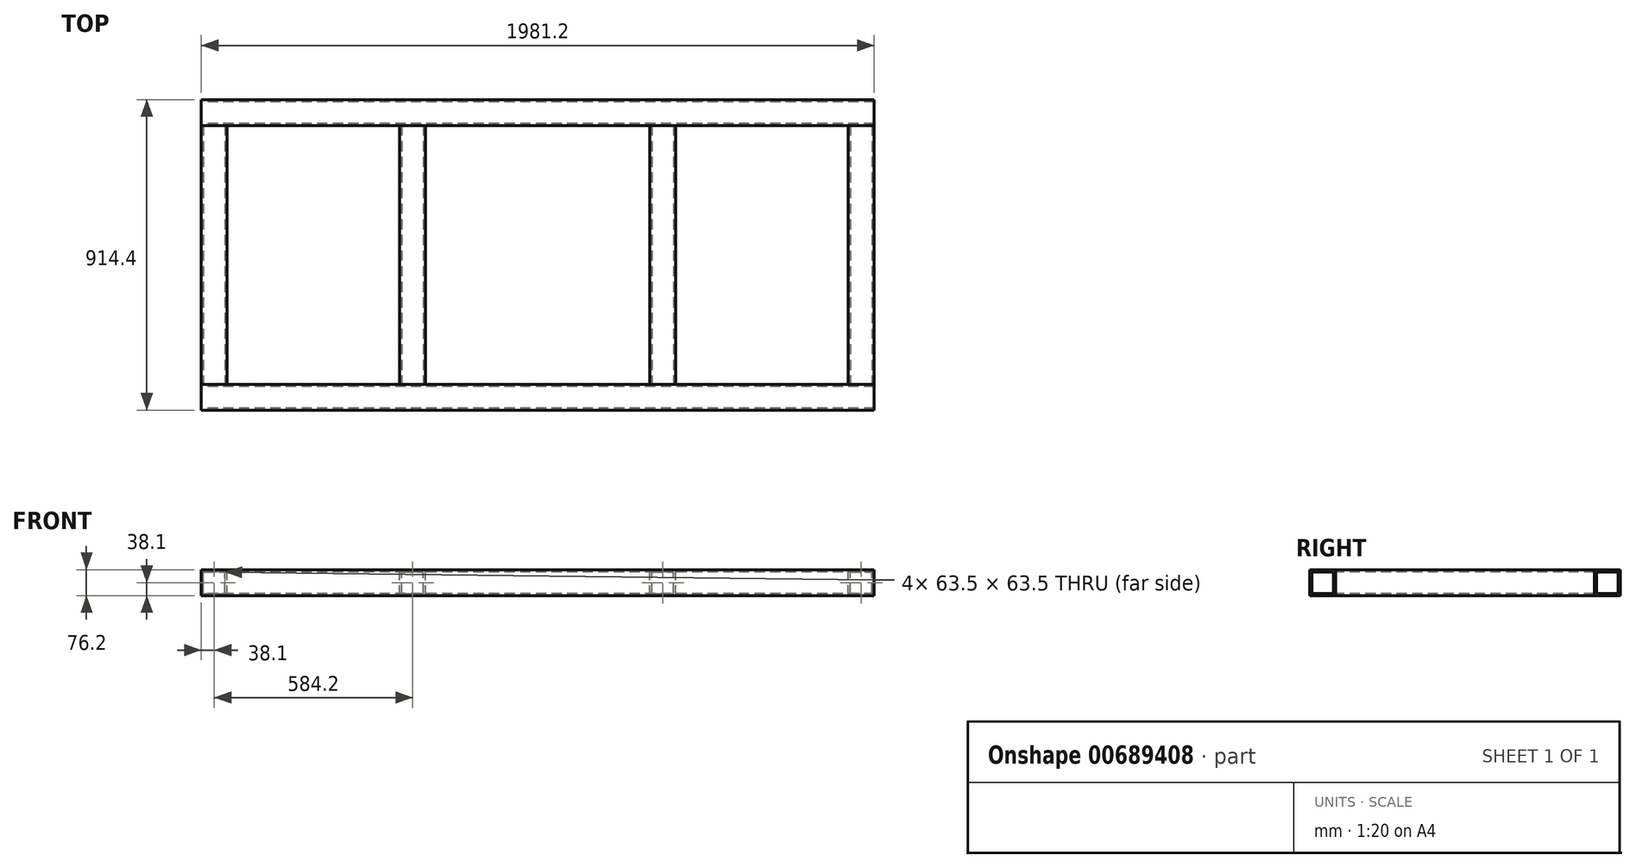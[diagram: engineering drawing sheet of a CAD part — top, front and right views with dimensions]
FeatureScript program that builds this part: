
annotation { "Feature Type Name" : "Feature", "Feature Type Description" : "" }
export const myFeature = defineFeature(function(context is Context, id is Id, definition is map)
    precondition{}
    {
        {
            var Q0;
            Q0=qCreatedBy(makeId("Right.planeOp"),FACE);
            var sketch = newSketch(context, id + "F0", { "sketchPlane" : qUnion([Q0])});
            skLineSegment(sketch, "E0.bottom", {"start": v(0, 0) * mm, "end": v(76.2, 0) * mm});
            skLineSegment(sketch, "E0.top", {"start": v(0, 76.2) * mm, "end": v(76.2, 76.2) * mm});
            skLineSegment(sketch, "E0.left", {"start": v(0, 0) * mm, "end": v(0, 76.2) * mm});
            skLineSegment(sketch, "E0.right", {"start": v(76.2, 0) * mm, "end": v(76.2, 76.2) * mm});
            skLineSegment(sketch, "E1.bottom", {"start": v(6.35, 6.35) * mm, "end": v(69.85, 6.35) * mm});
            skLineSegment(sketch, "E1.top", {"start": v(6.35, 69.85) * mm, "end": v(69.85, 69.85) * mm});
            skLineSegment(sketch, "E1.left", {"start": v(6.35, 6.35) * mm, "end": v(6.35, 69.85) * mm});
            skLineSegment(sketch, "E1.right", {"start": v(69.85, 6.35) * mm, "end": v(69.85, 69.85) * mm});
            skSolve(sketch);
        }
        {
            var Q0;
            Q0=makeQuery(id+"F0.imprint","IMPRINT",FACE,{"disambiguationData":[TD([[makeQuery(id+"F0.imprint","IMPRINT",EDGE,{"derivedFrom":sQuery(id+"F0.wireOp",EDGE,"E0.bottom")}),1.0]])]});
            extrude(context, id + "F1", {"entities" : qUnion([Q0]), "depth" : 1981.2 * mm, "offsetDistance" : 25.4 * mm});
        }
        {
            var Q0;
            Q0=makeQuery(id+"F1.opExtrude","SWEPT_BODY",BODY,{"disambiguationData":[OSD([sQuery(id+"F0.wireOp",EDGE,"E0.bottom"),sQuery(id+"F0.wireOp",EDGE,"E0.top"),sQuery(id+"F0.wireOp",EDGE,"E0.left"),sQuery(id+"F0.wireOp",EDGE,"E0.right"),sQuery(id+"F0.wireOp",EDGE,"E1.bottom"),sQuery(id+"F0.wireOp",EDGE,"E1.top"),sQuery(id+"F0.wireOp",EDGE,"E1.left"),sQuery(id+"F0.wireOp",EDGE,"E1.right")])]});
            var Q1;
            Q1=qCreatedBy(makeId("Front.planeOp"),FACE);
            transform(context, id + "F2", {"entities" : qUnion([Q0]), "transformType" : TransformType.TRANSLATION_DISTANCE, "transformDirection" : qUnion([Q1]), "distance" : 838.2 * mm, "oppositeDirection" : true, "makeCopy" : true});
        }
        {
            var Q0;
            Q0=qCreatedBy(makeId("Front.planeOp"),FACE);
            var sketch = newSketch(context, id + "F3", { "sketchPlane" : qUnion([Q0])});
            skLineSegment(sketch, "E2.bottom", {"start": v(0, 0) * mm, "end": v(76.2, 0) * mm});
            skLineSegment(sketch, "E2.top", {"start": v(0, 76.2) * mm, "end": v(76.2, 76.2) * mm});
            skLineSegment(sketch, "E2.left", {"start": v(0, 0) * mm, "end": v(0, 76.2) * mm});
            skLineSegment(sketch, "E2.right", {"start": v(76.2, 0) * mm, "end": v(76.2, 76.2) * mm});
            skLineSegment(sketch, "E3.bottom", {"start": v(6.35, 6.35) * mm, "end": v(69.85, 6.35) * mm});
            skLineSegment(sketch, "E3.top", {"start": v(6.35, 69.85) * mm, "end": v(69.85, 69.85) * mm});
            skLineSegment(sketch, "E3.left", {"start": v(6.35, 6.35) * mm, "end": v(6.35, 69.85) * mm});
            skLineSegment(sketch, "E3.right", {"start": v(69.85, 6.35) * mm, "end": v(69.85, 69.85) * mm});
            skSolve(sketch);
        }
        {
            var Q0;
            Q0=makeQuery(id+"F3.imprint","IMPRINT",FACE,{"disambiguationData":[TD([[makeQuery(id+"F3.imprint","IMPRINT",EDGE,{"derivedFrom":sQuery(id+"F3.wireOp",EDGE,"E2.bottom")}),1.0]])]});
            extrude(context, id + "F4", {"entities" : qUnion([Q0]), "oppositeDirection" : true, "depth" : 762 * mm, "offsetDistance" : 25.4 * mm});
        }
        {
            var Q0;
            Q0=makeQuery(id+"F4.opExtrude","SWEPT_BODY",BODY,{"disambiguationData":[OSD([sQuery(id+"F3.wireOp",EDGE,"E2.bottom"),sQuery(id+"F3.wireOp",EDGE,"E2.top"),sQuery(id+"F3.wireOp",EDGE,"E2.left"),sQuery(id+"F3.wireOp",EDGE,"E2.right"),sQuery(id+"F3.wireOp",EDGE,"E3.bottom"),sQuery(id+"F3.wireOp",EDGE,"E3.top"),sQuery(id+"F3.wireOp",EDGE,"E3.left"),sQuery(id+"F3.wireOp",EDGE,"E3.right")])]});
            var Q1;
            Q1=qCreatedBy(makeId("Front.planeOp"),FACE);
            transform(context, id + "F5", {"entities" : qUnion([Q0]), "transformType" : TransformType.TRANSLATION_DISTANCE, "transformDirection" : qUnion([Q1]), "distance" : 76.2 * mm, "oppositeDirection" : true, "makeCopy" : false});
        }
        {
            var Q0;
            Q0=makeQuery(id+"F4.opExtrude","SWEPT_BODY",BODY,{"disambiguationData":[OSD([sQuery(id+"F3.wireOp",EDGE,"E2.bottom"),sQuery(id+"F3.wireOp",EDGE,"E2.top"),sQuery(id+"F3.wireOp",EDGE,"E2.left"),sQuery(id+"F3.wireOp",EDGE,"E2.right"),sQuery(id+"F3.wireOp",EDGE,"E3.bottom"),sQuery(id+"F3.wireOp",EDGE,"E3.top"),sQuery(id+"F3.wireOp",EDGE,"E3.left"),sQuery(id+"F3.wireOp",EDGE,"E3.right")])]});
            var Q1;
            Q1=qCreatedBy(makeId("Right.planeOp"),FACE);
            transform(context, id + "F6", {"entities" : qUnion([Q0]), "transformType" : TransformType.TRANSLATION_DISTANCE, "transformDirection" : qUnion([Q1]), "distance" : 584.2 * mm, "makeCopy" : true});
        }
        {
            var Q0;
            Q0=makeQuery(id+"F6.opPattern","COPY",BODY,{"derivedFrom":makeQuery(id+"F4.opExtrude","SWEPT_BODY",BODY,{"disambiguationData":[OSD([sQuery(id+"F3.wireOp",EDGE,"E2.bottom"),sQuery(id+"F3.wireOp",EDGE,"E2.top"),sQuery(id+"F3.wireOp",EDGE,"E2.left"),sQuery(id+"F3.wireOp",EDGE,"E2.right"),sQuery(id+"F3.wireOp",EDGE,"E3.bottom"),sQuery(id+"F3.wireOp",EDGE,"E3.top"),sQuery(id+"F3.wireOp",EDGE,"E3.left"),sQuery(id+"F3.wireOp",EDGE,"E3.right")])]}),"instanceName":"1"});
            var Q1;
            Q1=qCreatedBy(makeId("Right.planeOp"),FACE);
            transform(context, id + "F7", {"entities" : qUnion([Q0]), "transformType" : TransformType.TRANSLATION_DISTANCE, "transformDirection" : qUnion([Q1]), "distance" : 736.6 * mm, "makeCopy" : true});
        }
        {
            var Q0;
            Q0=makeQuery(id+"F7.opPattern","COPY",BODY,{"derivedFrom":makeQuery(id+"F6.opPattern","COPY",BODY,{"derivedFrom":makeQuery(id+"F4.opExtrude","SWEPT_BODY",BODY,{"disambiguationData":[OSD([sQuery(id+"F3.wireOp",EDGE,"E2.bottom"),sQuery(id+"F3.wireOp",EDGE,"E2.top"),sQuery(id+"F3.wireOp",EDGE,"E2.left"),sQuery(id+"F3.wireOp",EDGE,"E2.right"),sQuery(id+"F3.wireOp",EDGE,"E3.bottom"),sQuery(id+"F3.wireOp",EDGE,"E3.top"),sQuery(id+"F3.wireOp",EDGE,"E3.left"),sQuery(id+"F3.wireOp",EDGE,"E3.right")])]}),"instanceName":"1"}),"instanceName":"1"});
            var Q1;
            Q1=qCreatedBy(makeId("Right.planeOp"),FACE);
            transform(context, id + "F8", {"entities" : qUnion([Q0]), "transformType" : TransformType.TRANSLATION_DISTANCE, "transformDirection" : qUnion([Q1]), "distance" : 584.2 * mm, "makeCopy" : true});
        }
    });
